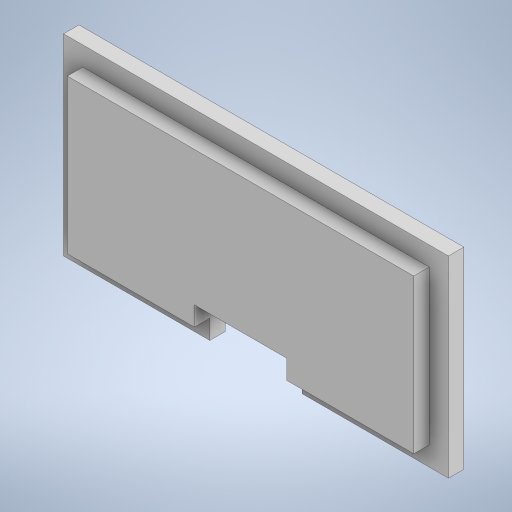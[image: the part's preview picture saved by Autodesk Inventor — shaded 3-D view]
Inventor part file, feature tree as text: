
AUTODESK INVENTOR PART (.ipt)
format: ipt  version: 2024.2 (Build 282272000, 272)  size: 232,960 bytes
history: native  units: mm
features: extrude x3, sketch x3
ambient origin geometry x8: Origin, YZ Plane, XZ Plane, XY Plane, X Axis, Y Axis, Z Axis, Center Point
bodies: Solid1 (feature_tree)
feature tree (6):
  extrude  "Extrusion1"  Depth=25.0mm
  extrude  "Extrusion2"  Depth=45.0mm
  extrude  "Extrusion3"  Depth=2.5mm
  sketch  "Sketch1"  dims[d0=50.0mm d1=25.0mm]
  sketch  "Sketch2"  dims[d2=2.0mm d3=0.0mm d4=45.0mm]
  sketch  "Sketch3"  dims[d5=20.0mm d6=2.5mm d7=2.5mm d8=2.0mm d9=0.0mm d10=12.0mm d11=5.0mm d12=19.0mm d13=0.0mm d14=0.0mm]
